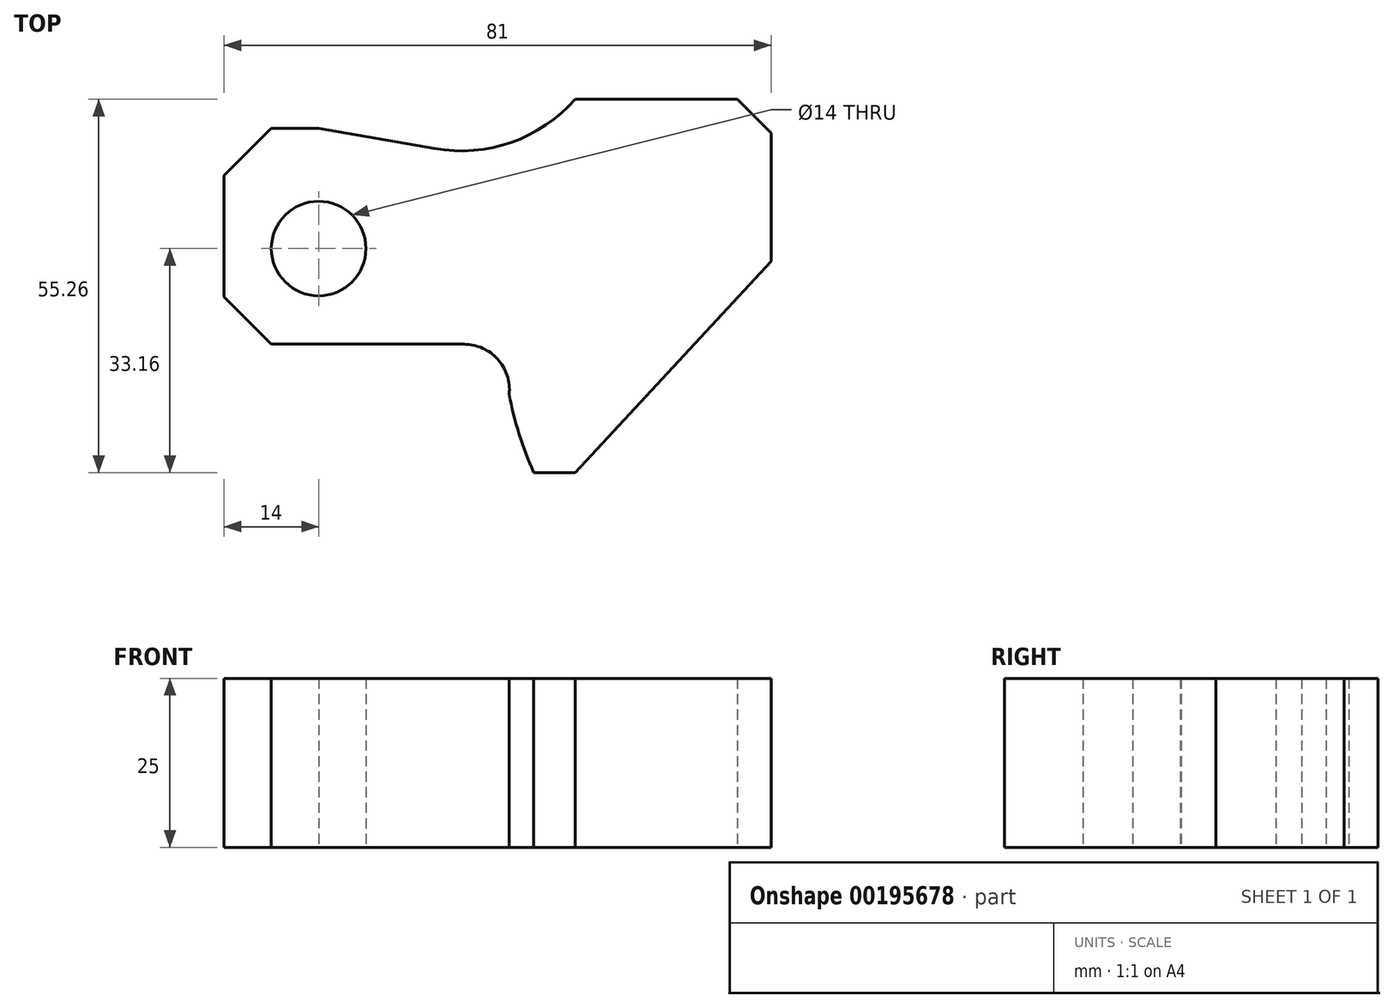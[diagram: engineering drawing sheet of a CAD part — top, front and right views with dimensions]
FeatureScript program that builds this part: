
annotation { "Feature Type Name" : "Feature", "Feature Type Description" : "" }
export const myFeature = defineFeature(function(context is Context, id is Id, definition is map)
    precondition{}
    {
        {
            var Q0;
            Q0=qCreatedBy(makeId("Top.planeOp"),FACE);
            var sketch = newSketch(context, id + "F0", { "sketchPlane" : qUnion([Q0])});
            skPoint(sketch, "E0.start.orphan", {"position": v(0, 57.52) * mm});
            skLineSegment(sketch, "E1", {"start": v(-14, -7.16) * mm, "end": v(-14, 10.84) * mm});
            skLineSegment(sketch, "E2", {"start": v(-14, 10.84) * mm, "end": v(-7, 17.84) * mm});
            skLineSegment(sketch, "E3", {"start": v(-7, 17.84) * mm, "end": v(0, 17.84) * mm});
            skLineSegment(sketch, "E4", {"start": v(38, 22.1) * mm, "end": v(62, 22.1) * mm});
            skLineSegment(sketch, "E5", {"start": v(62, 22.1) * mm, "end": v(67, 17.1) * mm});
            skLineSegment(sketch, "E6", {"start": v(67, 17.1) * mm, "end": v(67, -1.9) * mm});
            skLineSegment(sketch, "E7", {"start": v(-14, -7.16) * mm, "end": v(-7, -14.16) * mm});
            skLineSegment(sketch, "E8", {"start": v(-7, -14.16) * mm, "end": v(21.53, -14.16) * mm});
            skLineSegment(sketch, "E9", {"start": v(67, -1.9) * mm, "end": v(38, -33.16) * mm});
            skLineSegment(sketch, "E10", {"start": v(38, -33.16) * mm, "end": v(31.86, -33.16) * mm});
            skArc(sketch, "E11", {"start": v(28.21, -21.56) * mm, "mid": v(26.51, -16.38) * mm, "end": v(21.53, -14.16) * mm});
            skArc(sketch, "E12", {"start": v(28.21, -21.56) * mm, "mid": v(29.7, -27.47) * mm, "end": v(31.86, -33.16) * mm});
            skCircle(sketch, "E13", {"center": v(0, 0) * mm, "radius": 7 * mm});
            skLineSegment(sketch, "E14", {"start": v(0, 17.84) * mm, "end": v(17.16, 14.8) * mm});
            skArc(sketch, "E15", {"start": v(17.16, 14.8) * mm, "mid": v(28.53, 15.73) * mm, "end": v(38, 22.1) * mm});
            skSolve(sketch);
        }
        {
            var Q0;
            Q0 = qSketchRegion(id + "F0", true);
            extrude(context, id + "F1", {"entities" : qUnion([Q0]), "depth" : 25 * mm});
        }
    });
